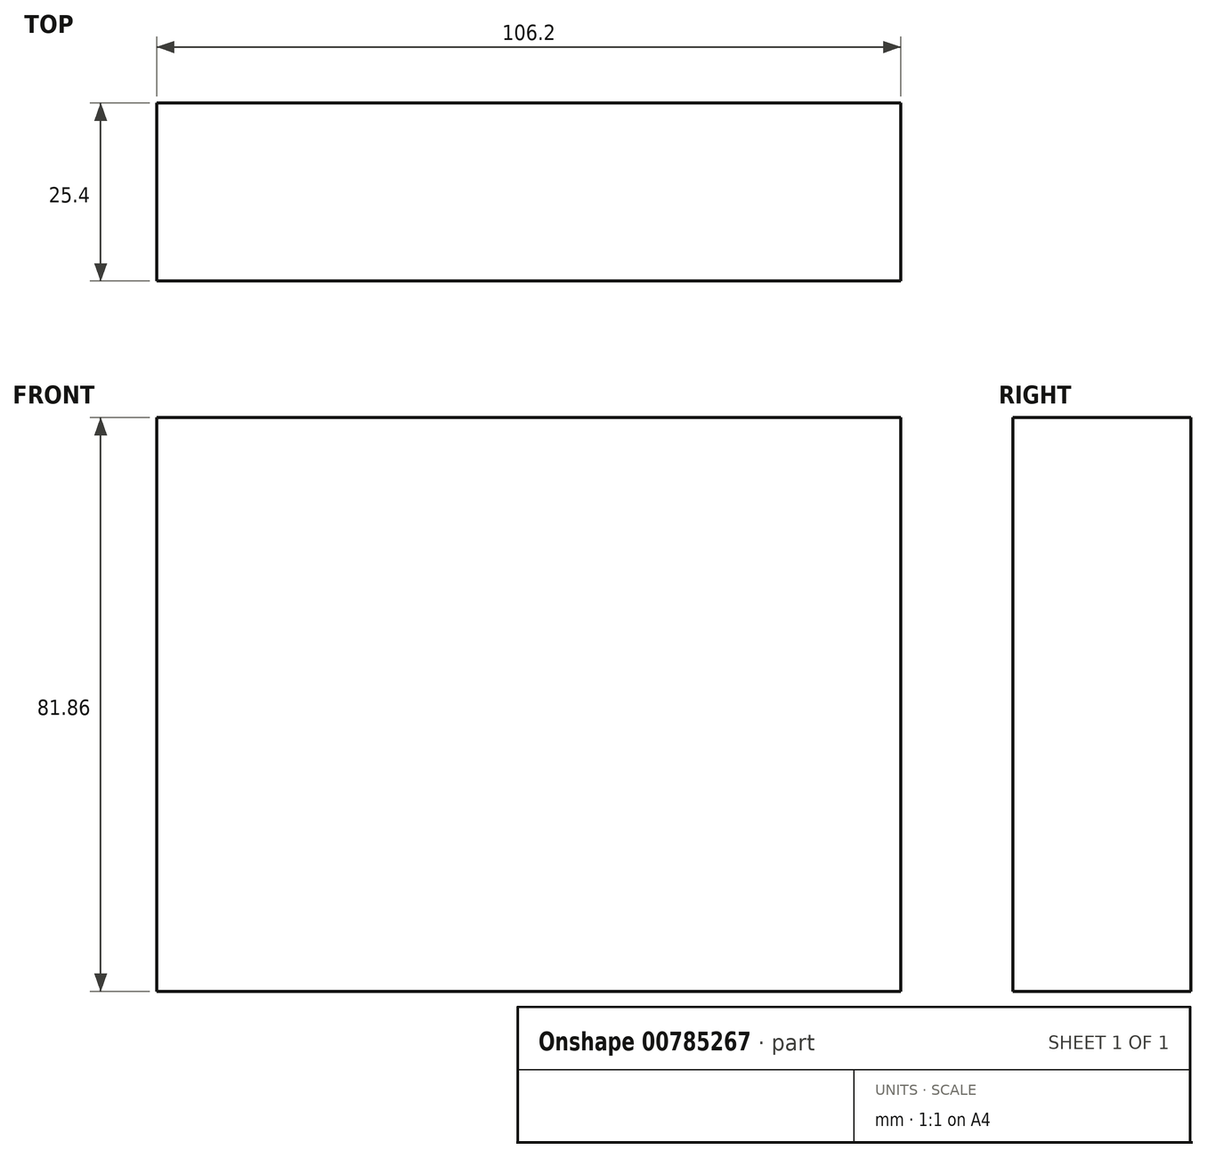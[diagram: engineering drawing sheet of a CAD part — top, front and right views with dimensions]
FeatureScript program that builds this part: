
annotation { "Feature Type Name" : "Feature", "Feature Type Description" : "" }
export const myFeature = defineFeature(function(context is Context, id is Id, definition is map)
    precondition{}
    {
        {
            var Q0;
            Q0=qCreatedBy(makeId("Front.planeOp"),FACE);
            var sketch = newSketch(context, id + "F0", { "sketchPlane" : qUnion([Q0])});
            skLineSegment(sketch, "E0.bottom", {"start": v(-53.1, 40.93) * mm, "end": v(53.1, 40.93) * mm});
            skLineSegment(sketch, "E0.top", {"start": v(-53.1, -40.93) * mm, "end": v(53.1, -40.93) * mm});
            skLineSegment(sketch, "E0.left", {"start": v(-53.1, 40.93) * mm, "end": v(-53.1, -40.93) * mm});
            skLineSegment(sketch, "E0.right", {"start": v(53.1, 40.93) * mm, "end": v(53.1, -40.93) * mm});
            skPoint(sketch, "E0.middle", {"position": v(0, 0) * mm});
            skSolve(sketch);
        }
        {
            var Q0;
            Q0 = qSketchRegion(id + "F0", true);
            extrude(context, id + "F1", {"entities" : qUnion([Q0]), "depth" : 25.4 * mm, "offsetDistance" : 25.4 * mm});
        }
    });
